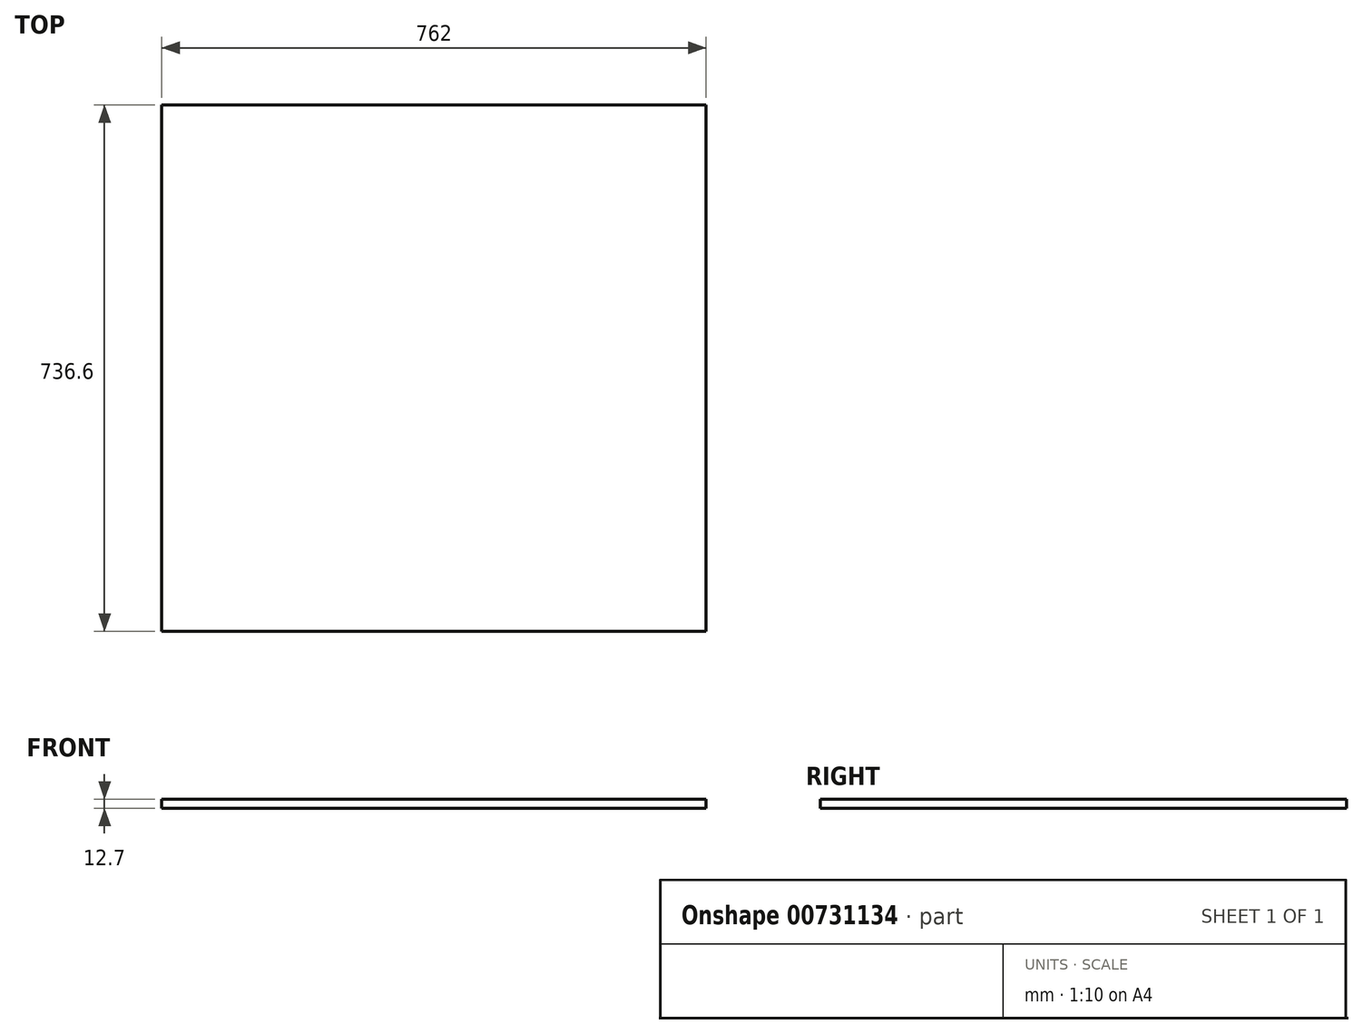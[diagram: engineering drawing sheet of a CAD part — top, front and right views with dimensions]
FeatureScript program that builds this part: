
annotation { "Feature Type Name" : "Feature", "Feature Type Description" : "" }
export const myFeature = defineFeature(function(context is Context, id is Id, definition is map)
    precondition{}
    {
        {
            var Q0;
            Q0=qCreatedBy(makeId("Top.planeOp"),FACE);
            var sketch = newSketch(context, id + "F0", { "sketchPlane" : qUnion([Q0])});
            skLineSegment(sketch, "E0.bottom", {"start": v(381, 368.3) * mm, "end": v(-381, 368.3) * mm});
            skLineSegment(sketch, "E0.top", {"start": v(381, -368.3) * mm, "end": v(-381, -368.3) * mm});
            skLineSegment(sketch, "E0.left", {"start": v(381, 368.3) * mm, "end": v(381, -368.3) * mm});
            skLineSegment(sketch, "E0.right", {"start": v(-381, 368.3) * mm, "end": v(-381, -368.3) * mm});
            skPoint(sketch, "E0.middle", {"position": v(0, 0) * mm});
            skSolve(sketch);
        }
        {
            var Q0;
            Q0 = qSketchRegion(id + "F0", true);
            extrude(context, id + "F1", {"entities" : qUnion([Q0]), "depth" : 12.7 * mm, "offsetDistance" : 25.4 * mm});
        }
    });
